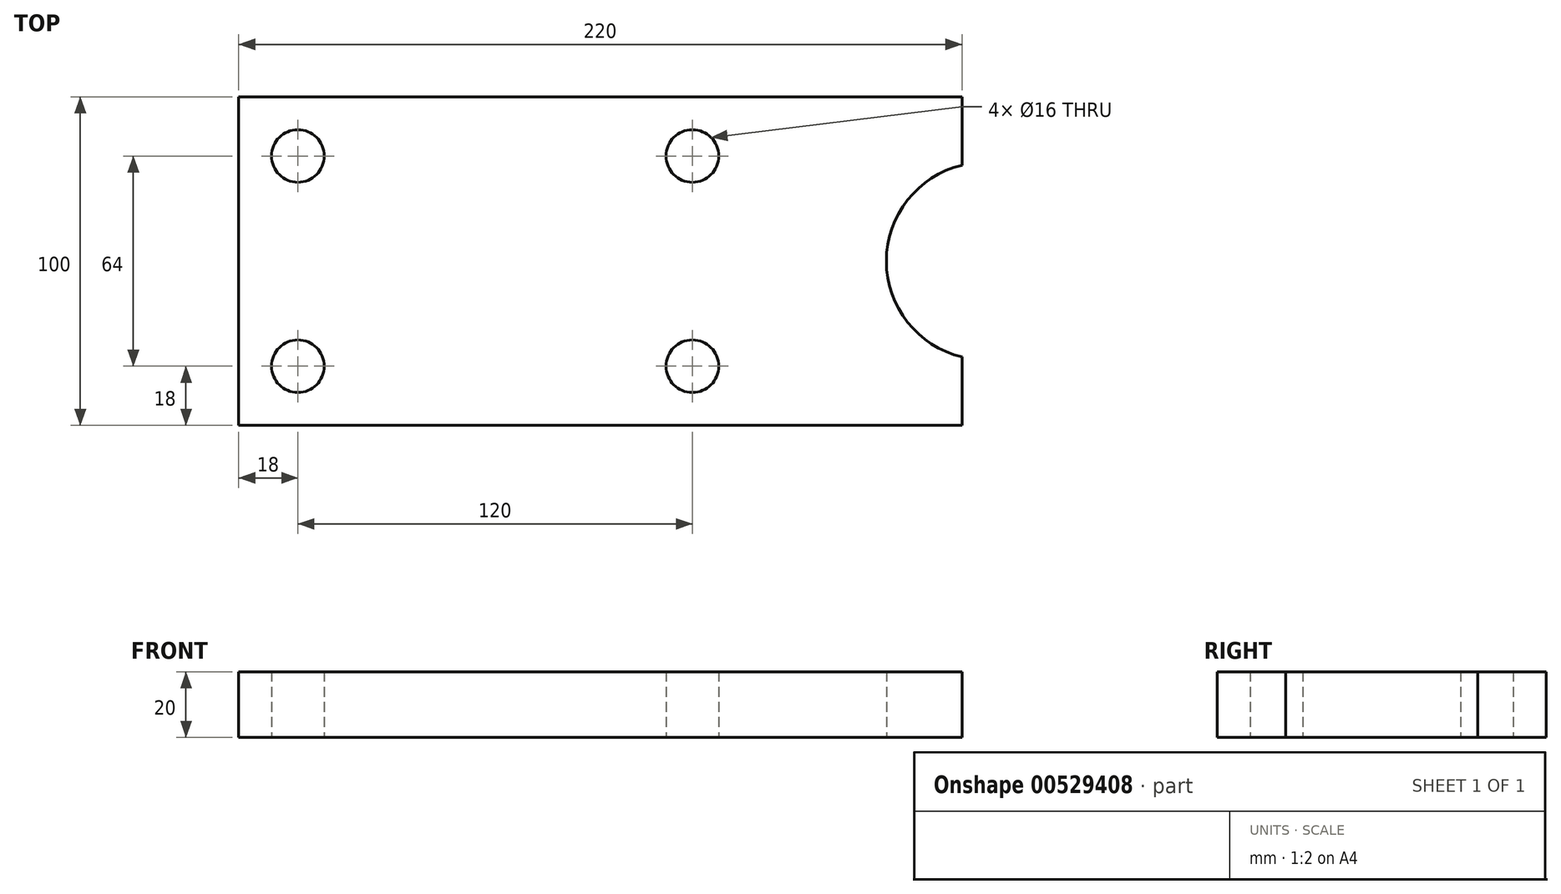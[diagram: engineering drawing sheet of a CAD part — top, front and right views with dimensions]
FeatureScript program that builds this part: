
annotation { "Feature Type Name" : "Feature", "Feature Type Description" : "" }
export const myFeature = defineFeature(function(context is Context, id is Id, definition is map)
    precondition{}
    {
        {
            var Q0;
            Q0=qCreatedBy(makeId("Top.planeOp"),FACE);
            var sketch = newSketch(context, id + "F0", { "sketchPlane" : qUnion([Q0])});
            skLineSegment(sketch, "E0.bottom", {"start": v(110, -50) * mm, "end": v(-110, -50) * mm});
            skLineSegment(sketch, "E0.top", {"start": v(110, 50) * mm, "end": v(-110, 50) * mm});
            skLineSegment(sketch, "E0.left", {"start": v(110, -50) * mm, "end": v(110, -29.17) * mm});
            skLineSegment(sketch, "E0.right", {"start": v(-110, -50) * mm, "end": v(-110, 50) * mm});
            skPoint(sketch, "E0.middle", {"position": v(0, 0) * mm});
            skLineSegment(sketch, "E1", {"start": v(-110, 0) * mm, "end": v(110, 0) * mm, "construction": true});
            skCircle(sketch, "E2", {"center": v(117, 0) * mm, "radius": 30 * mm});
            skLineSegment(sketch, "E3", {"start": v(-92, 0) * mm, "end": v(-92, 32) * mm, "construction": true});
            skLineSegment(sketch, "E4", {"start": v(28, 0) * mm, "end": v(28, 32) * mm, "construction": true});
            skLineSegment(sketch, "E5", {"start": v(-92, 32) * mm, "end": v(28, 32) * mm, "construction": true});
            skLineSegment(sketch, "E6", {"start": v(117, 0) * mm, "end": v(117, -50) * mm, "construction": true});
            skLineSegment(sketch, "E7", {"start": v(110, 29.17) * mm, "end": v(110, 50) * mm});
            skCircle(sketch, "E8", {"center": v(-92, 32) * mm, "radius": 8 * mm});
            skCircle(sketch, "E9", {"center": v(28, 32) * mm, "radius": 8 * mm});
            skCircle(sketch, "E10.MirrorC", {"center": v(-92, -32) * mm, "radius": 8 * mm});
            skCircle(sketch, "E11.MirrorC", {"center": v(28, -32) * mm, "radius": 8 * mm});
            skSolve(sketch);
        }
        {
            var Q0;
            Q0=makeQuery(id+"F0.imprint","IMPRINT",FACE,{"disambiguationData":[TD([[makeQuery(id+"F0.imprint","IMPRINT",EDGE,{"derivedFrom":sQuery(id+"F0.wireOp",EDGE,"E0.bottom")}),-1.0]])]});
            extrude(context, id + "F1", {"entities" : qUnion([Q0]), "endBound" : BoundingType.SYMMETRIC, "depth" : 20 * mm, "offsetDistance" : 25 * mm});
        }
    });
